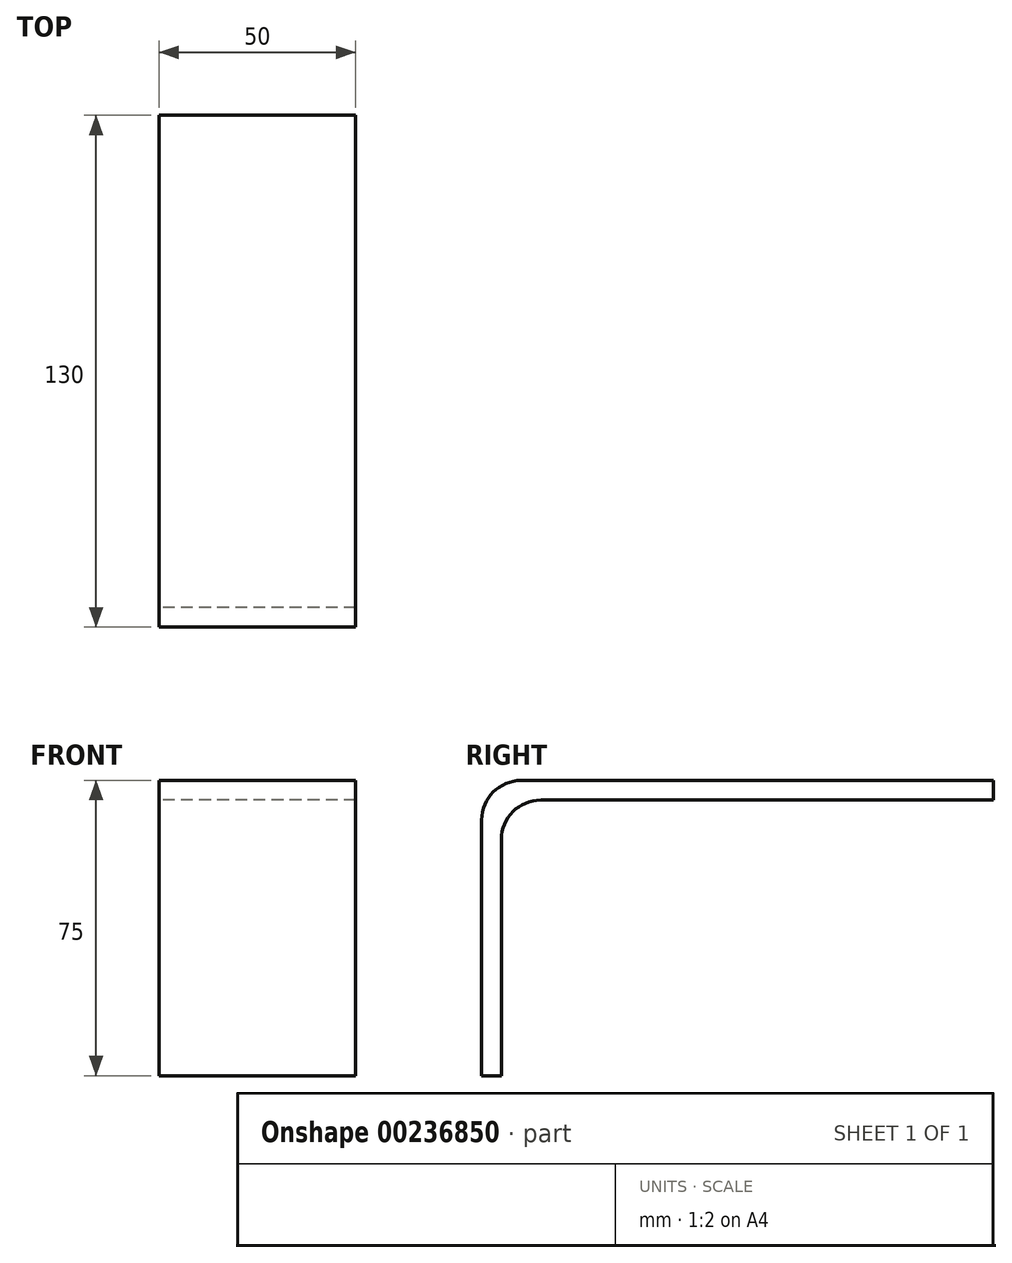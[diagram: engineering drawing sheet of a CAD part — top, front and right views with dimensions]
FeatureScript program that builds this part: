
annotation { "Feature Type Name" : "Feature", "Feature Type Description" : "" }
export const myFeature = defineFeature(function(context is Context, id is Id, definition is map)
    precondition{}
    {
        {
            var Q0;
            Q0=qCreatedBy(makeId("Right.planeOp"),FACE);
            var sketch = newSketch(context, id + "F0", { "sketchPlane" : qUnion([Q0])});
            skLineSegment(sketch, "E0.bottom", {"start": v(-34.29, 45.62) * mm, "end": v(85.71, 45.62) * mm});
            skLineSegment(sketch, "E0.top", {"start": v(-44.29, -29.38) * mm, "end": v(-39.29, -29.38) * mm});
            skLineSegment(sketch, "E0.left", {"start": v(-44.29, 35.62) * mm, "end": v(-44.29, -29.38) * mm});
            skLineSegment(sketch, "E0.right", {"start": v(85.71, 45.62) * mm, "end": v(85.71, 40.62) * mm});
            skLineSegment(sketch, "E1.bottom", {"start": v(-29.29, 40.62) * mm, "end": v(85.71, 40.62) * mm});
            skLineSegment(sketch, "E1.left", {"start": v(-39.29, 30.62) * mm, "end": v(-39.29, -29.38) * mm});
            skPoint(sketch, "E2.visualSharp", {"position": v(-44.29, 45.62) * mm});
            skArc(sketch, "E2.filletArc", {"start": v(-34.29, 45.62) * mm, "mid": v(-41.36, 42.69) * mm, "end": v(-44.29, 35.62) * mm});
            skPoint(sketch, "E3.visualSharp", {"position": v(-39.29, 40.62) * mm});
            skArc(sketch, "E3.filletArc", {"start": v(-29.29, 40.62) * mm, "mid": v(-36.36, 37.69) * mm, "end": v(-39.29, 30.62) * mm});
            skSolve(sketch);
        }
        {
            var Q0;
            Q0 = qSketchRegion(id + "F0", true);
            extrude(context, id + "F1", {"entities" : qUnion([Q0]), "depth" : 50 * mm});
        }
    });
